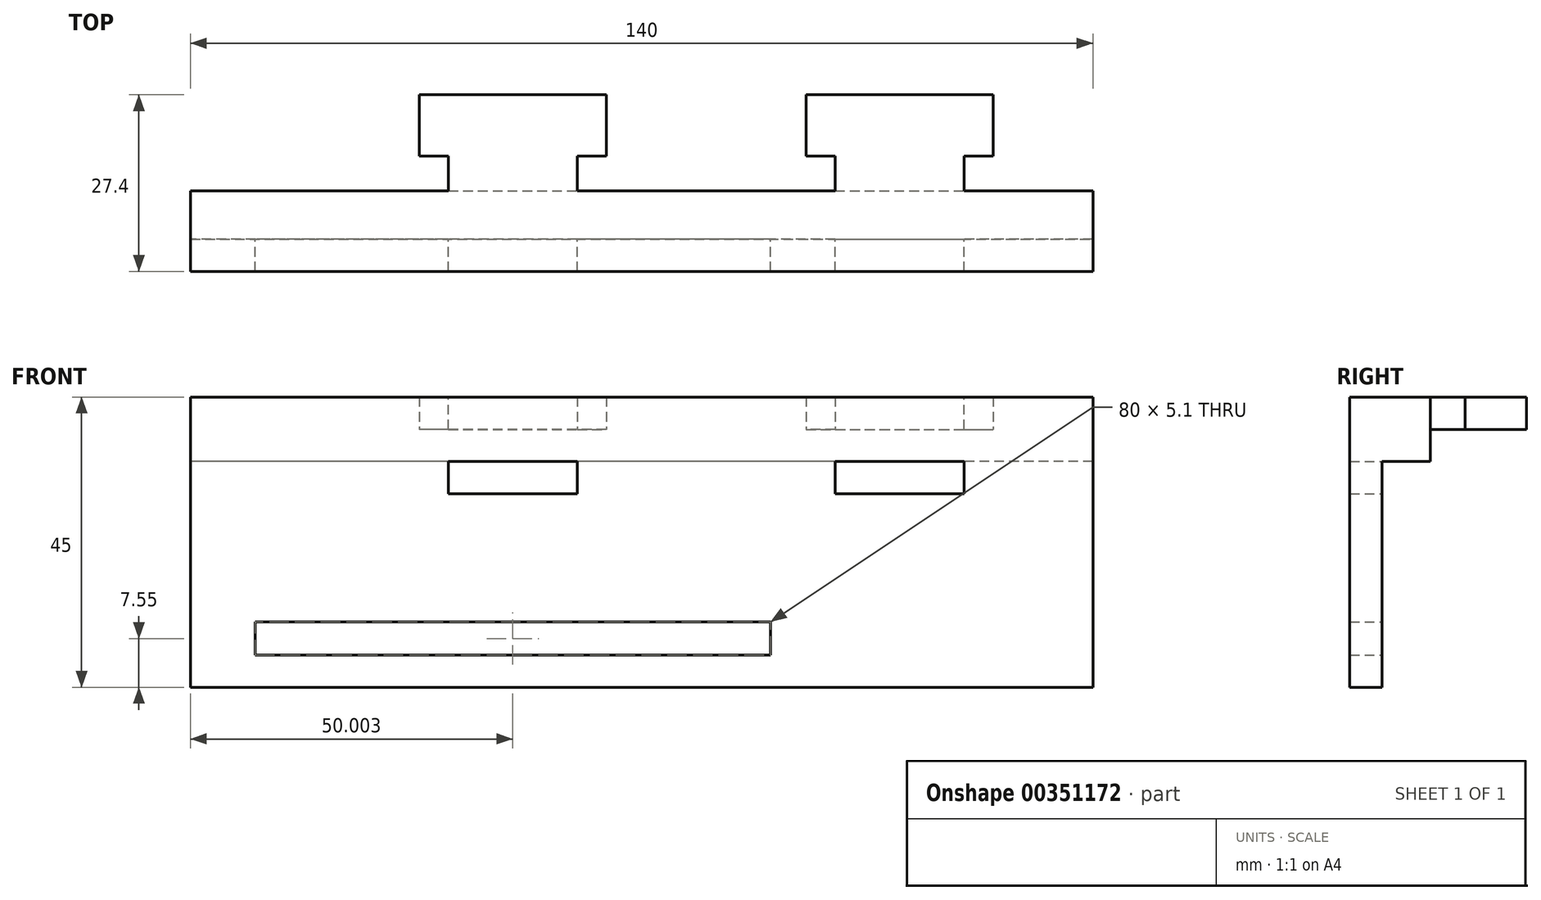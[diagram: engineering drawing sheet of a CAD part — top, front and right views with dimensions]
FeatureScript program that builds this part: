
annotation { "Feature Type Name" : "Feature", "Feature Type Description" : "" }
export const myFeature = defineFeature(function(context is Context, id is Id, definition is map)
    precondition{}
    {
        {
            var Q0;
            Q0=qCreatedBy(makeId("Front.planeOp"),FACE);
            var sketch = newSketch(context, id + "F0", { "sketchPlane" : qUnion([Q0])});
            skLineSegment(sketch, "E0.bottom", {"start": v(-54.56, 0) * mm, "end": v(85.44, 0) * mm});
            skLineSegment(sketch, "E0.top", {"start": v(-54.56, 45) * mm, "end": v(85.44, 45) * mm});
            skLineSegment(sketch, "E0.left", {"start": v(-54.56, 0) * mm, "end": v(-54.56, 45) * mm});
            skLineSegment(sketch, "E0.right", {"start": v(85.44, 0) * mm, "end": v(85.44, 45) * mm});
            skLineSegment(sketch, "E1", {"start": v(-54.56, 0) * mm, "end": v(-54.56, 5) * mm, "construction": true});
            skLineSegment(sketch, "E2", {"start": v(-54.56, 5) * mm, "end": v(-44.56, 5) * mm, "construction": true});
            skLineSegment(sketch, "E3", {"start": v(-44.56, 5) * mm, "end": v(-44.56, 10.1) * mm});
            skLineSegment(sketch, "E4", {"start": v(-44.56, 10.1) * mm, "end": v(35.44, 10.1) * mm});
            skLineSegment(sketch, "E5", {"start": v(35.44, 10.1) * mm, "end": v(35.44, 5) * mm});
            skLineSegment(sketch, "E6", {"start": v(35.44, 5) * mm, "end": v(-44.56, 5) * mm});
            skLineSegment(sketch, "E7", {"start": v(-54.56, 45) * mm, "end": v(-54.56, 40) * mm, "construction": true});
            skLineSegment(sketch, "E8", {"start": v(-54.56, 40) * mm, "end": v(-14.56, 40) * mm, "construction": true});
            skLineSegment(sketch, "E9", {"start": v(-14.56, 40) * mm, "end": v(-14.56, 35) * mm, "construction": true});
            skLineSegment(sketch, "E10", {"start": v(-14.56, 35) * mm, "end": v(5.44, 35) * mm});
            skLineSegment(sketch, "E11", {"start": v(5.44, 35) * mm, "end": v(5.44, 30) * mm});
            skLineSegment(sketch, "E12", {"start": v(5.44, 30) * mm, "end": v(-14.56, 30) * mm});
            skLineSegment(sketch, "E13", {"start": v(-14.56, 30) * mm, "end": v(-14.56, 35) * mm});
            skLineSegment(sketch, "E14", {"start": v(-14.56, 40) * mm, "end": v(5.44, 40) * mm});
            skLineSegment(sketch, "E15", {"start": v(5.44, 40) * mm, "end": v(5.44, 45) * mm});
            skLineSegment(sketch, "E16", {"start": v(5.44, 45) * mm, "end": v(-14.56, 45) * mm});
            skLineSegment(sketch, "E17", {"start": v(-14.56, 45) * mm, "end": v(-14.56, 40) * mm});
            skLineSegment(sketch, "E18", {"start": v(5.44, 40) * mm, "end": v(45.44, 40) * mm, "construction": true});
            skLineSegment(sketch, "E19", {"start": v(45.44, 40) * mm, "end": v(65.44, 40) * mm});
            skLineSegment(sketch, "E20", {"start": v(65.44, 40) * mm, "end": v(65.44, 45) * mm});
            skLineSegment(sketch, "E21", {"start": v(65.44, 45) * mm, "end": v(45.44, 45) * mm});
            skLineSegment(sketch, "E22", {"start": v(45.44, 45) * mm, "end": v(45.44, 40) * mm});
            skLineSegment(sketch, "E23", {"start": v(45.44, 40) * mm, "end": v(45.44, 35) * mm, "construction": true});
            skLineSegment(sketch, "E24", {"start": v(45.44, 35) * mm, "end": v(45.44, 30) * mm});
            skLineSegment(sketch, "E25", {"start": v(45.44, 30) * mm, "end": v(65.44, 30) * mm});
            skLineSegment(sketch, "E26", {"start": v(65.44, 30) * mm, "end": v(65.44, 35) * mm});
            skLineSegment(sketch, "E27", {"start": v(65.44, 35) * mm, "end": v(45.44, 35) * mm});
            skSolve(sketch);
        }
        {
            var Q0;
            Q0=makeQuery(id+"F0.imprint","IMPRINT",FACE,{"disambiguationData":[TD([[makeQuery(id+"F0.imprint","IMPRINT",EDGE,{"derivedFrom":sQuery(id+"F0.wireOp",EDGE,"E0.bottom")}),1.0]])]});
            var Q1;
            Q1=makeQuery(id+"F0.imprint","IMPRINT",FACE,{"disambiguationData":[TD([[makeQuery(id+"F0.imprint","IMPRINT",EDGE,{"derivedFrom":sQuery(id+"F0.wireOp",EDGE,"E19")}),1.0]])]});
            var Q2;
            Q2=makeQuery(id+"F0.imprint","IMPRINT",FACE,{"disambiguationData":[TD([[makeQuery(id+"F0.imprint","IMPRINT",EDGE,{"derivedFrom":sQuery(id+"F0.wireOp",EDGE,"E14")}),1.0]])]});
            extrude(context, id + "F1", {"entities" : qUnion([Q0, Q1, Q2]), "depth" : 5 * mm});
        }
        {
            var Q0;
            Q0=makeQuery(id+"F1.opExtrude","CAP_FACE",FACE,{"disambiguationData":[OSD([sQuery(id+"F0.wireOp",EDGE,"E0.bottom"),sQuery(id+"F0.wireOp",EDGE,"E0.top"),sQuery(id+"F0.wireOp",EDGE,"E0.left"),sQuery(id+"F0.wireOp",EDGE,"E0.right"),sQuery(id+"F0.wireOp",EDGE,"E3"),sQuery(id+"F0.wireOp",EDGE,"E4"),sQuery(id+"F0.wireOp",EDGE,"E5"),sQuery(id+"F0.wireOp",EDGE,"E6"),sQuery(id+"F0.wireOp",EDGE,"E10"),sQuery(id+"F0.wireOp",EDGE,"E11"),sQuery(id+"F0.wireOp",EDGE,"E12"),sQuery(id+"F0.wireOp",EDGE,"E13"),sQuery(id+"F0.wireOp",EDGE,"E16"),sQuery(id+"F0.wireOp",EDGE,"E21"),sQuery(id+"F0.wireOp",EDGE,"E24"),sQuery(id+"F0.wireOp",EDGE,"E25"),sQuery(id+"F0.wireOp",EDGE,"E26"),sQuery(id+"F0.wireOp",EDGE,"E27")])],"isStart":true});
            var sketch = newSketch(context, id + "F2", { "sketchPlane" : qUnion([Q0])});
            skPoint(sketch, "E28", {"position": v(54.56, 45) * mm});
            skPoint(sketch, "E29", {"position": v(-85.44, 45) * mm});
            skPoint(sketch, "E30", {"position": v(-85.44, 0) * mm});
            skPoint(sketch, "E31", {"position": v(54.56, 0) * mm});
            skPoint(sketch, "E32", {"position": v(14.56, 45) * mm});
            skPoint(sketch, "E33", {"position": v(-5.44, 45) * mm});
            skPoint(sketch, "E34", {"position": v(-45.44, 45) * mm});
            skPoint(sketch, "E35", {"position": v(-65.44, 45) * mm});
            skLineSegment(sketch, "E36", {"start": v(-5.44, 45) * mm, "end": v(-5.44, 40) * mm});
            skLineSegment(sketch, "E37", {"start": v(-5.44, 40) * mm, "end": v(14.56, 40) * mm});
            skLineSegment(sketch, "E38", {"start": v(14.56, 40) * mm, "end": v(14.56, 45) * mm});
            skLineSegment(sketch, "E39", {"start": v(-5.44, 45) * mm, "end": v(14.56, 45) * mm});
            skLineSegment(sketch, "E40", {"start": v(-5.44, 45) * mm, "end": v(-45.44, 45) * mm, "construction": true});
            skLineSegment(sketch, "E41", {"start": v(-45.44, 45) * mm, "end": v(-45.44, 40) * mm});
            skLineSegment(sketch, "E42", {"start": v(-45.44, 40) * mm, "end": v(-65.44, 40) * mm});
            skLineSegment(sketch, "E43", {"start": v(-65.44, 40) * mm, "end": v(-65.44, 45) * mm});
            skLineSegment(sketch, "E44", {"start": v(-45.44, 45) * mm, "end": v(-65.44, 45) * mm});
            skLineSegment(sketch, "E45", {"start": v(-65.44, 40) * mm, "end": v(-85.44, 40) * mm});
            skLineSegment(sketch, "E46", {"start": v(-85.44, 40) * mm, "end": v(-85.44, 45) * mm});
            skLineSegment(sketch, "E47", {"start": v(54.56, 45) * mm, "end": v(54.56, 40) * mm});
            skLineSegment(sketch, "E48", {"start": v(54.56, 40) * mm, "end": v(-45.44, 40) * mm});
            skLineSegment(sketch, "E49", {"start": v(-85.44, 40) * mm, "end": v(-85.44, 35) * mm});
            skLineSegment(sketch, "E50", {"start": v(-85.44, 35) * mm, "end": v(54.56, 35) * mm});
            skLineSegment(sketch, "E51", {"start": v(54.56, 35) * mm, "end": v(54.56, 40) * mm});
            skSolve(sketch);
        }
        {
            var Q0;
            {var subQ0=sQuery(id+"F2.wireOp",EDGE,"E43");Q0=makeQuery(id+"F2.imprint","IMPRINT",FACE,{"disambiguationData":[TD([[makeQuery(id+"F2.imprint","IMPRINT",EDGE,{"derivedFrom":subQ0}),1.0]])]});}
            var Q1;
            {var subQ0=sQuery(id+"F2.wireOp",EDGE,"E36");Q1=makeQuery(id+"F2.imprint","IMPRINT",FACE,{"disambiguationData":[TD([[makeQuery(id+"F2.imprint","IMPRINT",EDGE,{"derivedFrom":subQ0}),-1.0]])]});}
            var Q2;
            {var subQ0=sQuery(id+"F2.wireOp",EDGE,"E38");Q2=makeQuery(id+"F2.imprint","IMPRINT",FACE,{"disambiguationData":[TD([[makeQuery(id+"F2.imprint","IMPRINT",EDGE,{"derivedFrom":subQ0}),-1.0]])]});}
            extrude(context, id + "F3", {"entities" : qUnion([Q0, Q1, Q2]), "operationType" : NewBodyOperationType.ADD, "depth" : 7.5 * mm});
        }
        {
            var Q0;
            Q0=makeQuery(id+"F2.imprint","IMPRINT",FACE,{"disambiguationData":[TD([[makeQuery(id+"F2.imprint","IMPRINT",EDGE,{"derivedFrom":sQuery(id+"F2.wireOp",EDGE,"E41")}),-1.0]])]});
            var Q1;
            {var subQ0=sQuery(id+"F2.wireOp",EDGE,"E36");Q1=makeQuery(id+"F2.imprint","IMPRINT",FACE,{"disambiguationData":[TD([[makeQuery(id+"F2.imprint","IMPRINT",EDGE,{"derivedFrom":subQ0}),1.0]])]});}
            extrude(context, id + "F4", {"entities" : qUnion([Q0, Q1]), "operationType" : NewBodyOperationType.ADD, "depth" : 22.4 * mm});
        }
        {
            var Q0;
            Q0=makeQuery(id+"F4.opExtrude","CAP_FACE",FACE,{"disambiguationData":[OSD([sQuery(id+"F2.wireOp",EDGE,"E41"),sQuery(id+"F2.wireOp",EDGE,"E42"),sQuery(id+"F2.wireOp",EDGE,"E43"),sQuery(id+"F2.wireOp",EDGE,"E44")])],"isStart":false});
            var sketch = newSketch(context, id + "F5", { "sketchPlane" : qUnion([Q0])});
            skLineSegment(sketch, "E52.bottom", {"start": v(-65.44, 45) * mm, "end": v(-69.94, 45) * mm});
            skLineSegment(sketch, "E52.top", {"start": v(-65.44, 40) * mm, "end": v(-69.94, 40) * mm});
            skLineSegment(sketch, "E52.left", {"start": v(-65.44, 45) * mm, "end": v(-65.44, 40) * mm});
            skLineSegment(sketch, "E52.right", {"start": v(-69.94, 45) * mm, "end": v(-69.94, 40) * mm});
            skLineSegment(sketch, "E53.bottom", {"start": v(-45.44, 45) * mm, "end": v(-40.94, 45) * mm});
            skLineSegment(sketch, "E53.top", {"start": v(-45.44, 40) * mm, "end": v(-40.94, 40) * mm});
            skLineSegment(sketch, "E53.left", {"start": v(-45.44, 45) * mm, "end": v(-45.44, 40) * mm});
            skLineSegment(sketch, "E53.right", {"start": v(-40.94, 45) * mm, "end": v(-40.94, 40) * mm});
            skSolve(sketch);
        }
        {
            var Q0;
            Q0=makeQuery(id+"F5.imprint","IMPRINT",FACE,{"disambiguationData":[TD([[makeQuery(id+"F5.imprint","IMPRINT",EDGE,{"derivedFrom":sQuery(id+"F5.wireOp",EDGE,"E52.bottom")}),1.0]])]});
            var Q1;
            Q1=makeQuery(id+"F5.imprint","IMPRINT",FACE,{"disambiguationData":[TD([[makeQuery(id+"F5.imprint","IMPRINT",EDGE,{"derivedFrom":sQuery(id+"F5.wireOp",EDGE,"E53.bottom")}),-1.0]])]});
            extrude(context, id + "F6", {"entities" : qUnion([Q0, Q1]), "operationType" : NewBodyOperationType.ADD, "depth" : -9.5 * mm});
        }
        {
            var Q0;
            Q0=makeQuery(id+"F4.opExtrude","CAP_FACE",FACE,{"disambiguationData":[OSD([sQuery(id+"F2.wireOp",EDGE,"E36"),sQuery(id+"F2.wireOp",EDGE,"E38"),sQuery(id+"F2.wireOp",EDGE,"E39"),sQuery(id+"F2.wireOp",EDGE,"E48")])],"isStart":false});
            var sketch = newSketch(context, id + "F7", { "sketchPlane" : qUnion([Q0])});
            skLineSegment(sketch, "E54.bottom", {"start": v(14.56, 45) * mm, "end": v(19.06, 45) * mm});
            skLineSegment(sketch, "E54.top", {"start": v(14.56, 40) * mm, "end": v(19.06, 40) * mm});
            skLineSegment(sketch, "E54.left", {"start": v(14.56, 45) * mm, "end": v(14.56, 40) * mm});
            skLineSegment(sketch, "E54.right", {"start": v(19.06, 45) * mm, "end": v(19.06, 40) * mm});
            skLineSegment(sketch, "E55.bottom", {"start": v(-5.44, 45) * mm, "end": v(-9.94, 45) * mm});
            skLineSegment(sketch, "E55.top", {"start": v(-5.44, 40) * mm, "end": v(-9.94, 40) * mm});
            skLineSegment(sketch, "E55.left", {"start": v(-5.44, 45) * mm, "end": v(-5.44, 40) * mm});
            skLineSegment(sketch, "E55.right", {"start": v(-9.94, 45) * mm, "end": v(-9.94, 40) * mm});
            skSolve(sketch);
        }
        {
            var Q0;
            Q0=makeQuery(id+"F7.imprint","IMPRINT",FACE,{"disambiguationData":[TD([[makeQuery(id+"F7.imprint","IMPRINT",EDGE,{"derivedFrom":sQuery(id+"F7.wireOp",EDGE,"E55.bottom")}),1.0]])]});
            var Q1;
            Q1=makeQuery(id+"F7.imprint","IMPRINT",FACE,{"disambiguationData":[TD([[makeQuery(id+"F7.imprint","IMPRINT",EDGE,{"derivedFrom":sQuery(id+"F7.wireOp",EDGE,"E54.bottom")}),-1.0]])]});
            extrude(context, id + "F8", {"entities" : qUnion([Q0, Q1]), "operationType" : NewBodyOperationType.ADD, "depth" : -9.5 * mm});
        }
        {
            var Q0;
            {var subQ8=sQuery(id+"F2.wireOp",EDGE,"E42");Q0=makeQuery(id+"F2.imprint","IMPRINT",FACE,{"disambiguationData":[TD([[makeQuery(id+"F2.imprint","IMPRINT",EDGE,{"derivedFrom":subQ8}),1.0]])]});}
            extrude(context, id + "F9", {"entities" : qUnion([Q0]), "operationType" : NewBodyOperationType.ADD, "depth" : 7.5 * mm});
        }
    });
